# Revit family: Ladder_Rung_Kattsafe_Angled_Caged_AccessPlatform
name_source: partatom
category: Specialty Equipment
units: mm (PartAtom-declared; Revit-internal decimal feet)

## family parameters
Always vertical = Yes
Cut with Voids When Loaded = No
Enable Cutting in Views = No
Maintain Annotation Orientation = No
OmniClass Number = 23.17.23.15
Part Type = Normal
Room Calculation Point = No
Round Connector Dimension = Use Diameter
Shared = No
Work Plane-Based = No

## types (2) — shared parameters
Angle = 75.00°
Assembly Code = E1090100
ElementType = Ladder
Export Type to IFC As = IfcBuildingElementProxy
IfcExportAs = IfcBuildingElementProxy
IfcExportType = USERDEFINED
Manufacturer = Kattsafe®
ManufacturerOverallDepth = 3789 mm
ManufacturerURLProductSpecific = https://kattsafe.com.au
Material = Aluminum_Kattsafe_Satin
ModifiedIssue = 20250224 $
Type Comments = Ladder - Angled - Rung - Caged - Access Platform
Type IFC Predefined Type = USERDEFINED
URL = https://kattsafe.com.au
Uniclass2015Code = Pr_25_30_85_02
Uniclass2015Title = Access ladders
Uniclass2015Version = Products v1.35
zero-valued in all types: Default Elevation

## per-type parameters (varying)
| type | Description | LowerLadder | ManufacturerSpecCode | Model |
| Landing (RL36) | Angled caged ladder with midway landing and access platform | Yes | RL36 | RL36 |
| Suspended Landing (RL36S) | Angled caged ladder with suspended midway landing and access platform. Available with metal deck and concrete floor mounting options | No | RL36S | RL36S |

## geometry (parser evidence)
native form markers: Sweep x36
no freeform markers — native parametric forms only
